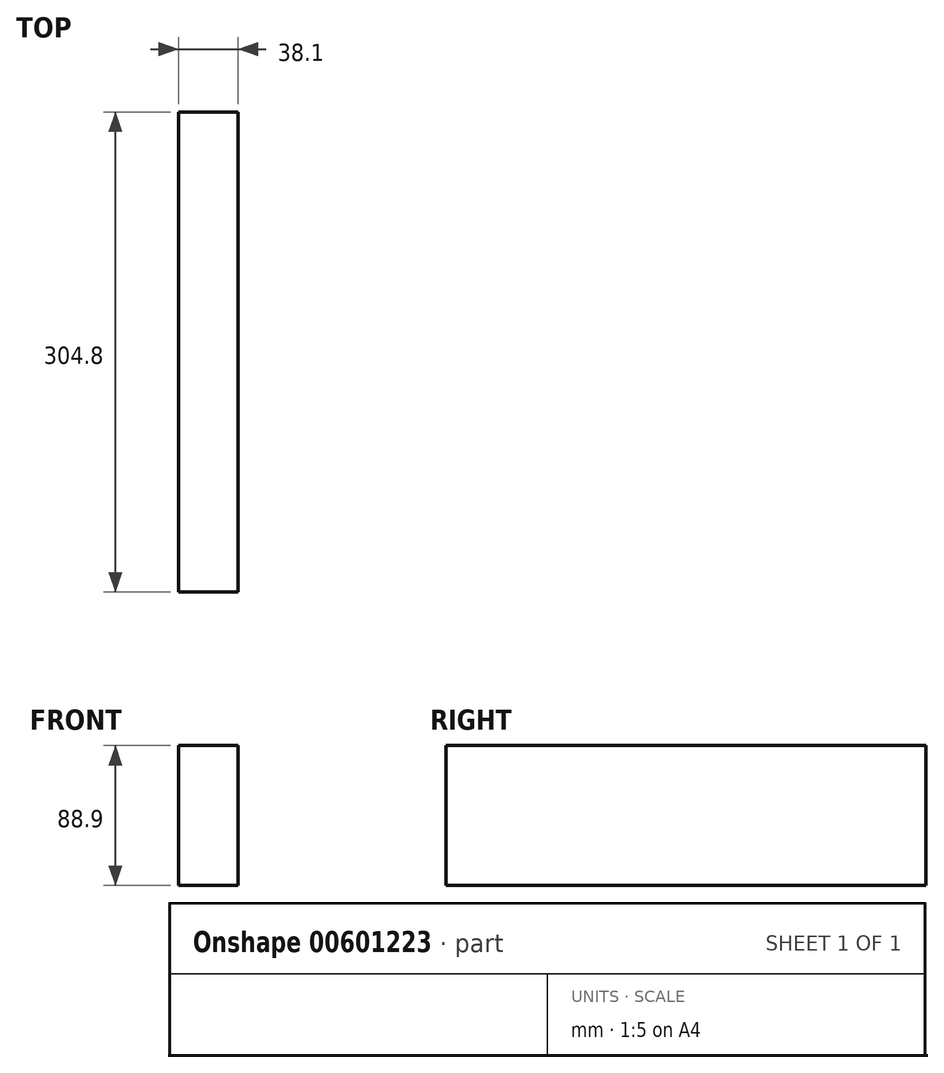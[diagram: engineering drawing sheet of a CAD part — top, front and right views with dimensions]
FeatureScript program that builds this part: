
annotation { "Feature Type Name" : "Feature", "Feature Type Description" : "" }
export const myFeature = defineFeature(function(context is Context, id is Id, definition is map)
    precondition{}
    {
        {
            var Q0;
            Q0=qCreatedBy(makeId("Front.planeOp"),FACE);
            var sketch = newSketch(context, id + "F0", { "sketchPlane" : qUnion([Q0])});
            skLineSegment(sketch, "E0.bottom", {"start": v(-45.54, 129.75) * mm, "end": v(-7.44, 129.75) * mm});
            skLineSegment(sketch, "E0.top", {"start": v(-45.54, 40.85) * mm, "end": v(-7.44, 40.85) * mm});
            skLineSegment(sketch, "E0.left", {"start": v(-45.54, 129.75) * mm, "end": v(-45.54, 40.85) * mm});
            skLineSegment(sketch, "E0.right", {"start": v(-7.44, 129.75) * mm, "end": v(-7.44, 40.85) * mm});
            skSolve(sketch);
        }
        {
            var Q0;
            Q0=makeQuery(id+"F0.imprint","IMPRINT",FACE,{"disambiguationData":[TD([[makeQuery(id+"F0.imprint","IMPRINT",EDGE,{"derivedFrom":sQuery(id+"F0.wireOp",EDGE,"E0.bottom")}),-1.0]])]});
            extrude(context, id + "F1", {"entities" : qUnion([Q0]), "depth" : 304.8 * mm, "offsetDistance" : 25.4 * mm});
        }
    });
